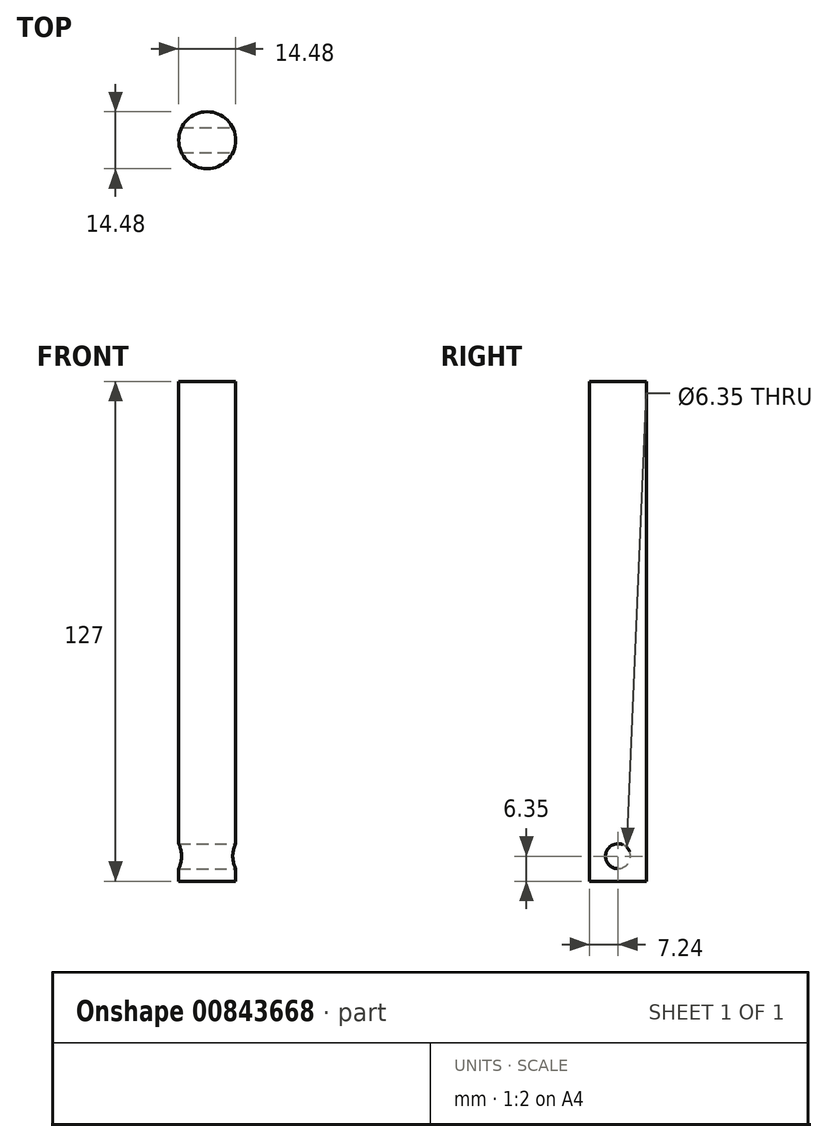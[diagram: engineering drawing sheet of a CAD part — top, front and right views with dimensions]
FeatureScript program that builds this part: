
annotation { "Feature Type Name" : "Feature", "Feature Type Description" : "" }
export const myFeature = defineFeature(function(context is Context, id is Id, definition is map)
    precondition{}
    {
        {
            var Q0;
            Q0=qCreatedBy(makeId("Top.planeOp"),FACE);
            var sketch = newSketch(context, id + "F0", { "sketchPlane" : qUnion([Q0])});
            skCircle(sketch, "E0", {"center": v(0, 0) * mm, "radius": 7.24 * mm});
            skSolve(sketch);
        }
        {
            var Q0;
            Q0 = qSketchRegion(id + "F0", true);
            extrude(context, id + "F1", {"entities" : qUnion([Q0]), "depth" : 127 * mm, "offsetDistance" : 25.4 * mm});
        }
        {
            var Q0;
            Q0=qCreatedBy(makeId("Right.planeOp"),FACE);
            var sketch = newSketch(context, id + "F2", { "sketchPlane" : qUnion([Q0])});
            skCircle(sketch, "E1", {"center": v(0, 6.35) * mm, "radius": 3.18 * mm});
            skSolve(sketch);
        }
        {
            var Q0;
            Q0 = qSketchRegion(id + "F2", true);
            extrude(context, id + "F3", {"entities" : qUnion([Q0]), "operationType" : NewBodyOperationType.REMOVE, "oppositeDirection" : true, "depth" : 25.4 * mm, "offsetDistance" : 25.4 * mm, "hasSecondDirection" : true, "secondDirectionOppositeDirection" : false, "secondDirectionDepth" : 25.4 * mm});
        }
    });
